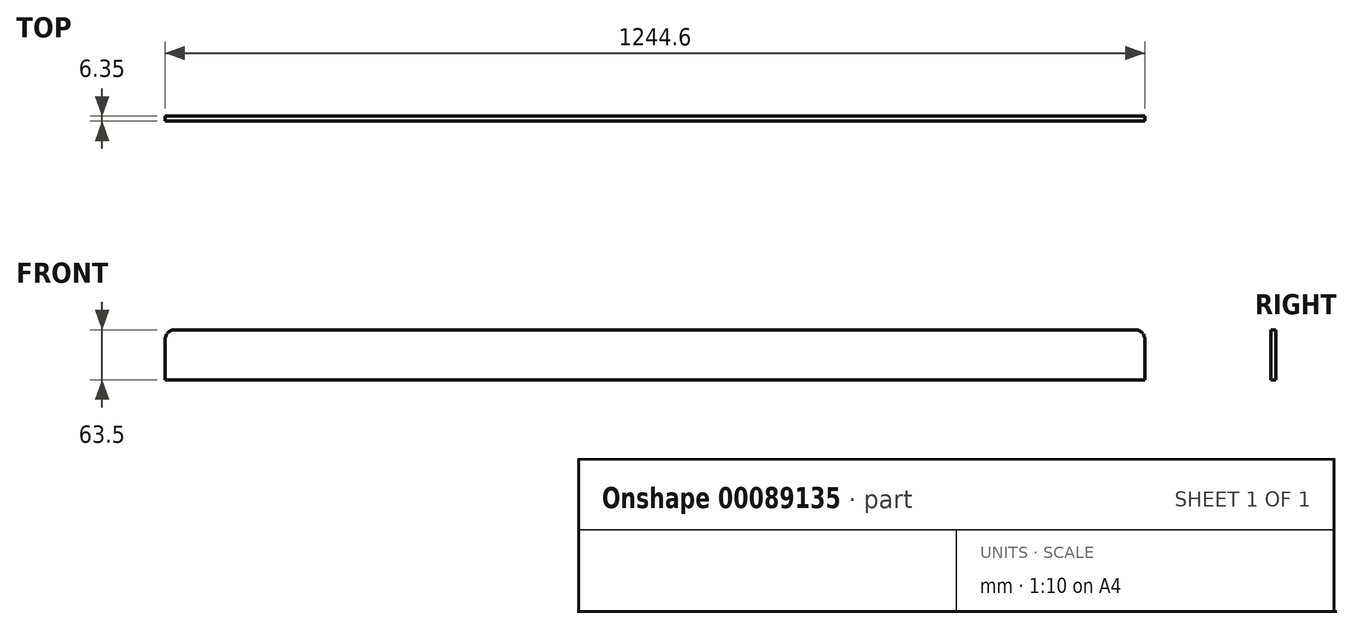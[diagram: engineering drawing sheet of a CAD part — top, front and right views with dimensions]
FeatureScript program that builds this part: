
annotation { "Feature Type Name" : "Feature", "Feature Type Description" : "" }
export const myFeature = defineFeature(function(context is Context, id is Id, definition is map)
    precondition{}
    {
        {
            var Q0;
            Q0=qCreatedBy(makeId("Front.planeOp"),FACE);
            var sketch = newSketch(context, id + "F0", { "sketchPlane" : qUnion([Q0])});
            skLineSegment(sketch, "E0.bottom", {"start": v(-622.3, 0) * mm, "end": v(622.3, 0) * mm});
            skLineSegment(sketch, "E0.top", {"start": v(-622.3, 63.5) * mm, "end": v(622.3, 63.5) * mm});
            skLineSegment(sketch, "E0.left", {"start": v(-622.3, 0) * mm, "end": v(-622.3, 63.5) * mm});
            skLineSegment(sketch, "E0.right", {"start": v(622.3, 0) * mm, "end": v(622.3, 63.5) * mm});
            skLineSegment(sketch, "E1", {"start": v(0, -294.84) * mm, "end": v(0, 651.1) * mm, "construction": true});
            skSolve(sketch);
        }
        {
            var Q0;
            Q0 = qSketchRegion(id + "F0", true);
            extrude(context, id + "F1", {"entities" : qUnion([Q0]), "depth" : 6.35 * mm});
        }
        {
            var Q0;
            Q0=makeQuery(id+"F1.opExtrude","SWEPT_EDGE",EDGE,{"disambiguationData":[OSD([sQuery(id+"F0.wireOp",EDGE,"E0.top"),sQuery(id+"F0.wireOp",EDGE,"E0.left")])]});
            var Q1;
            Q1=makeQuery(id+"F1.opExtrude","SWEPT_EDGE",EDGE,{"disambiguationData":[OSD([sQuery(id+"F0.wireOp",EDGE,"E0.top"),sQuery(id+"F0.wireOp",EDGE,"E0.right")])]});
            fillet(context, id + "F2", {"entities" : qUnion([Q0, Q1]), "radius" : 12.7 * mm, "tangentPropagation" : true, "allowEdgeOverflow" : false});
        }
    });
